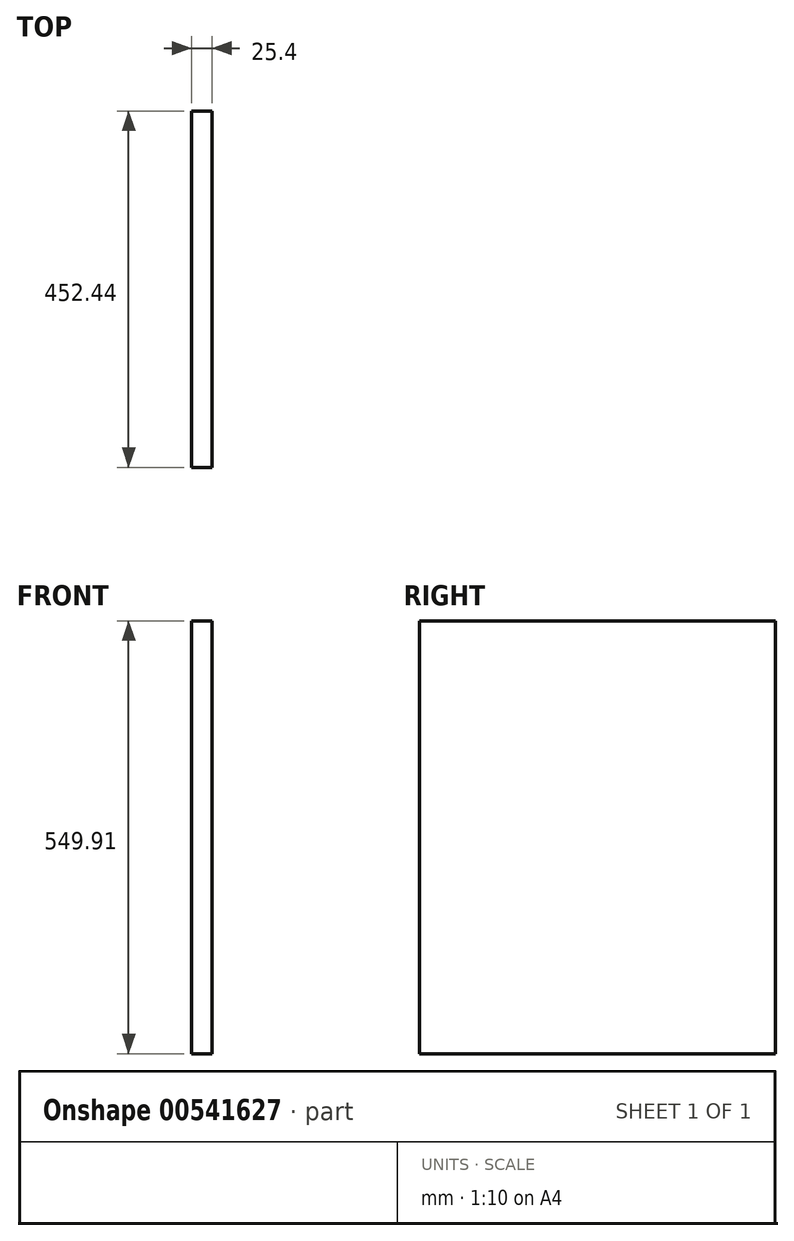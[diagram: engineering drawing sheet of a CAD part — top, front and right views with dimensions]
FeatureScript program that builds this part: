
annotation { "Feature Type Name" : "Feature", "Feature Type Description" : "" }
export const myFeature = defineFeature(function(context is Context, id is Id, definition is map)
    precondition{}
    {
        {
            var Q0;
            Q0=qCreatedBy(makeId("Right.planeOp"),FACE);
            var sketch = newSketch(context, id + "F0", { "sketchPlane" : qUnion([Q0])});
            skLineSegment(sketch, "E0.bottom", {"start": v(37.87, -1088.25) * mm, "end": v(490.31, -1088.25) * mm});
            skLineSegment(sketch, "E0.top", {"start": v(37.87, -1638.16) * mm, "end": v(490.31, -1638.16) * mm});
            skLineSegment(sketch, "E0.left", {"start": v(37.87, -1088.25) * mm, "end": v(37.87, -1638.16) * mm});
            skLineSegment(sketch, "E0.right", {"start": v(490.31, -1088.25) * mm, "end": v(490.31, -1638.16) * mm});
            skSolve(sketch);
        }
        {
            var Q0;
            Q0=makeQuery(id+"F0.imprint","IMPRINT",FACE,{"disambiguationData":[TD([[makeQuery(id+"F0.imprint","IMPRINT",EDGE,{"derivedFrom":sQuery(id+"F0.wireOp",EDGE,"E0.bottom")}),-1.0]])]});
            extrude(context, id + "F1", {"entities" : qUnion([Q0]), "depth" : 25.4 * mm, "offsetDistance" : 25.4 * mm});
        }
    });
